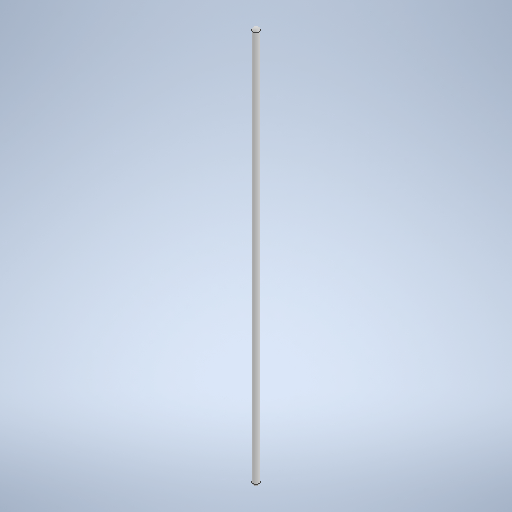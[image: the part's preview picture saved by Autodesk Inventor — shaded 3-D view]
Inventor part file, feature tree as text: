
AUTODESK INVENTOR PART (.ipt)
format: ipt  version: 2025 (Build 290162000, 162)  size: 252,416 bytes
history: native  units: in
note: dims shown in document units (in); Inventor stores cm internally (conversion verified against a paired STEP export)
features: extrude x1, fillet x1, sketch x1
ambient origin geometry x8: Origin, YZ Plane, XZ Plane, XY Plane, X Axis, Y Axis, Z Axis, Center Point
bodies: Solid1 (feature_tree)
feature tree (3):
  extrude  "Extrusion1"  Depth=0.1575in TaperAngle=0.0deg
  fillet  "Fillet1"  Radius=0.1575in
  sketch  "Sketch1"  dims[d1=0.315in d2=19.685in d3=0.0in d4=0.1575in]
